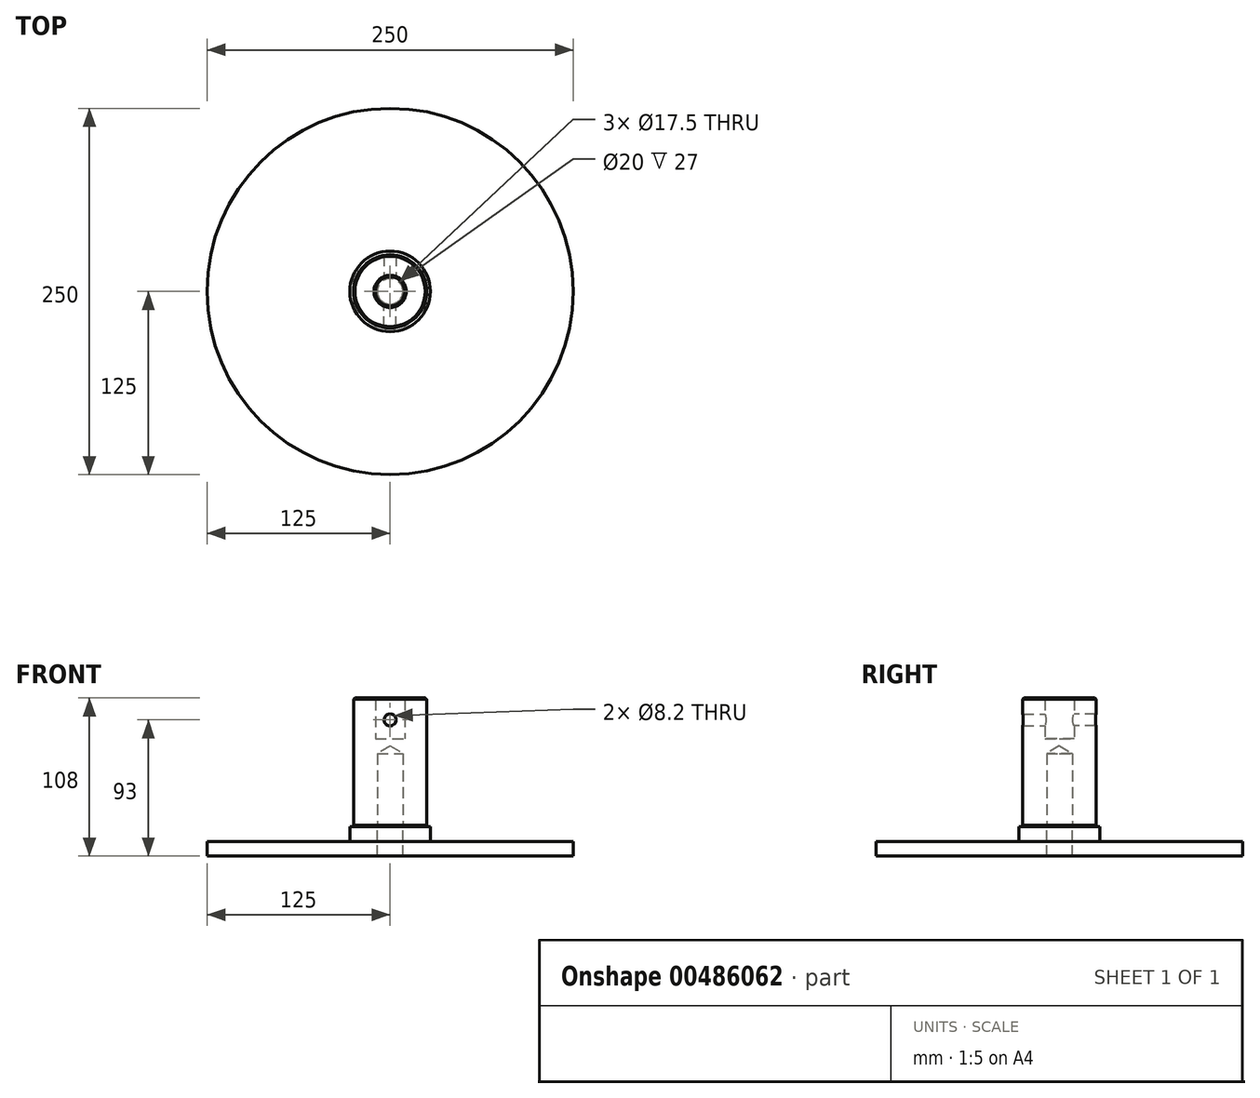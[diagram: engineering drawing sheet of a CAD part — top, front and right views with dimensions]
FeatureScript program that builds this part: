
annotation { "Feature Type Name" : "Feature", "Feature Type Description" : "" }
export const myFeature = defineFeature(function(context is Context, id is Id, definition is map)
    precondition{}
    {
        {
            var Q0;
            Q0=qCreatedBy(makeId("Front.planeOp"),FACE);
            var sketch = newSketch(context, id + "F0", { "sketchPlane" : qUnion([Q0])});
            skLineSegment(sketch, "E0.bottom", {"start": v(25, 0) * mm, "end": v(10, 0) * mm});
            skLineSegment(sketch, "E0.top", {"start": v(25, -48) * mm, "end": v(-25, -48) * mm});
            skLineSegment(sketch, "E0.left", {"start": v(25, 0) * mm, "end": v(25, -48) * mm});
            skLineSegment(sketch, "E0.right", {"start": v(-25, 0) * mm, "end": v(-25, -48) * mm});
            skLineSegment(sketch, "E1.top", {"start": v(10, -28) * mm, "end": v(-10, -28) * mm});
            skLineSegment(sketch, "E1.left", {"start": v(10, 0) * mm, "end": v(10, -28) * mm});
            skLineSegment(sketch, "E1.right", {"start": v(-10, 0) * mm, "end": v(-10, -28) * mm});
            skLineSegment(sketch, "E2", {"start": v(0, -137.33) * mm, "end": v(0, 23.92) * mm});
            skPoint(sketch, "E2.startSnap0", {"position": v(0, 0) * mm});
            skLineSegment(sketch, "E3.trimOffspring", {"start": v(-10, 0) * mm, "end": v(-25, 0) * mm});
            skPoint(sketch, "E4", {"position": v(0, -15) * mm});
            skLineSegment(sketch, "E5.bottom", {"start": v(-9.1, -48) * mm, "end": v(25, -48) * mm});
            skLineSegment(sketch, "E6.top", {"start": v(25, -88) * mm, "end": v(-25, -88) * mm});
            skLineSegment(sketch, "E6.left", {"start": v(25, -48) * mm, "end": v(25, -88) * mm});
            skLineSegment(sketch, "E6.right", {"start": v(-25, -48) * mm, "end": v(-25, -88) * mm});
            skSolve(sketch);
        }
        {
            var Q0;
            Q0=makeQuery(id+"F0.imprint","IMPRINT",FACE,{"disambiguationData":[TD([[makeQuery(id+"F0.imprint","IMPRINT",EDGE,{"derivedFrom":sQuery(id+"F0.wireOp",EDGE,"E0.bottom")}),1.0]])]});
            var Q1;
            Q1=sQuery(id+"F0.wireOp",EDGE,"E2");
            revolve(context, id + "F1", {"entities" : qUnion([Q0]), "axis" : qUnion([Q1]), "revolveType" : RevolveType.FULL});
        }
        {
            var Q0;
            Q0=makeQuery(id+"F1.opRevolve","SWEPT_EDGE",EDGE,{"disambiguationData":[OSD([sQuery(id+"F0.wireOp",EDGE,"E0.bottom"),sQuery(id+"F0.wireOp",EDGE,"E1.left")])]});
            var Q1;
            Q1=makeQuery(id+"F1.opRevolve","SWEPT_EDGE",EDGE,{"disambiguationData":[OSD([sQuery(id+"F0.wireOp",EDGE,"E0.bottom"),sQuery(id+"F0.wireOp",EDGE,"E0.left")])]});
            chamfer(context, id + "F2", {"entities" : qUnion([Q0, Q1]), "width" : 1 * mm, "tangentPropagation" : true});
        }
        {
            var Q0;
            Q0=sQuery(id+"F0.wireOp",VERTEX,"E4");
            var Q1;
            Q1=makeQuery(id+"F1.opRevolve","SWEPT_BODY",BODY,{"disambiguationData":[OSD([sQuery(id+"F0.wireOp",EDGE,"E0.bottom"),sQuery(id+"F0.wireOp",EDGE,"E0.top"),sQuery(id+"F0.wireOp",EDGE,"E0.left"),sQuery(id+"F0.wireOp",EDGE,"E1.top"),sQuery(id+"F0.wireOp",EDGE,"E1.left"),sQuery(id+"F0.wireOp",EDGE,"E2")])]});
            hole(context, id + "F3", {"style" : HoleStyle.SIMPLE, "endStyle" : HoleEndStyle.THROUGH, "oppositeDirection" : true, "standardTappedOrClearance" : lookupTablePath({ "standard" : "ISO", "size" : "8.2", "type" : "Drilled" }), "standardBlindInLast" : lookupTablePath({ "standard" : "ISO", "size" : "8.2", "type" : "Drilled" }), "holeDiameter" : 8.2 * mm, "isTappedThrough" : true, "tappedDepth" : 12 * mm, "tapClearance" : 3, "startFromSketch" : true, "locations" : qUnion([Q0]), "scope" : qUnion([Q1])});
        }
        {
            var Q0;
            Q0=sQuery(id+"F0.wireOp",VERTEX,"E4");
            var Q1;
            Q1=makeQuery(id+"F1.opRevolve","SWEPT_BODY",BODY,{"disambiguationData":[OSD([sQuery(id+"F0.wireOp",EDGE,"E0.bottom"),sQuery(id+"F0.wireOp",EDGE,"E0.top"),sQuery(id+"F0.wireOp",EDGE,"E0.left"),sQuery(id+"F0.wireOp",EDGE,"E1.top"),sQuery(id+"F0.wireOp",EDGE,"E1.left"),sQuery(id+"F0.wireOp",EDGE,"E2")])]});
            hole(context, id + "F4", {"style" : HoleStyle.SIMPLE, "endStyle" : HoleEndStyle.THROUGH, "standardTappedOrClearance" : lookupTablePath({ "standard" : "ISO", "size" : "8.2", "type" : "Drilled" }), "standardBlindInLast" : lookupTablePath({ "standard" : "ISO", "size" : "8.2", "type" : "Drilled" }), "holeDiameter" : 8.2 * mm, "isTappedThrough" : true, "tappedDepth" : 12 * mm, "tapClearance" : 3, "startFromSketch" : true, "locations" : qUnion([Q0]), "scope" : qUnion([Q1])});
        }
        {
            var Q0;
            {var subQ0=sQuery(id+"F0.wireOp",EDGE,"E6.right");Q0=makeQuery(id+"F0.imprint","IMPRINT",FACE,{"disambiguationData":[TD([[makeQuery(id+"F0.imprint","IMPRINT",EDGE,{"derivedFrom":subQ0}),1.0]])]});}
            var Q1;
            Q1=sQuery(id+"F0.wireOp",EDGE,"E2");
            revolve(context, id + "F5", {"operationType" : NewBodyOperationType.ADD, "entities" : qUnion([Q0]), "axis" : qUnion([Q1]), "revolveType" : RevolveType.FULL});
        }
        {
            var Q0;
            Q0=makeQuery(id+"F5.opRevolve","SWEPT_EDGE",EDGE,{"disambiguationData":[OSD([sQuery(id+"F0.wireOp",EDGE,"E6.top"),sQuery(id+"F0.wireOp",EDGE,"E6.left")])]});
            chamfer(context, id + "F6", {"entities" : qUnion([Q0]), "width" : 1 * mm, "tangentPropagation" : true});
        }
        {
            var Q0;
            Q0=makeQuery(id+"F5.opRevolve","SWEPT_FACE",FACE,{"disambiguationData":[OSD([sQuery(id+"F0.wireOp",EDGE,"E6.top")])]});
            var sketch = newSketch(context, id + "F7", { "sketchPlane" : qUnion([Q0])});
            skPoint(sketch, "E7", {"position": v(0, 0) * mm});
            skCircle(sketch, "E8", {"center": v(0, 0) * mm, "radius": 27.5 * mm});
            skSolve(sketch);
        }
        {
            var Q0;
            Q0=sQuery(id+"F7.wireOp",VERTEX,"E7");
            var Q1;
            Q1=makeQuery(id+"F1.opRevolve","SWEPT_BODY",BODY,{"disambiguationData":[OSD([sQuery(id+"F0.wireOp",EDGE,"E0.bottom"),sQuery(id+"F0.wireOp",EDGE,"E0.left"),sQuery(id+"F0.wireOp",EDGE,"E1.top"),sQuery(id+"F0.wireOp",EDGE,"E1.left"),sQuery(id+"F0.wireOp",EDGE,"E2"),sQuery(id+"F0.wireOp",EDGE,"E0.top")])]});
            hole(context, id + "F8", {"style" : HoleStyle.SIMPLE, "endStyle" : HoleEndStyle.BLIND, "standardTappedOrClearance" : lookupTablePath({ "standard" : "ISO", "engagement" : "75%", "pitch" : "2.5 mm", "size" : "M20", "type" : "Tapped" }), "standardBlindInLast" : lookupTablePath({ "standard" : "ISO", "engagement" : "75%", "pitch" : "2.5 mm", "size" : "M20", "type" : "Tapped" }), "holeDiameter" : 17.5 * mm, "majorDiameter" : 20 * mm, "showTappedDepth" : true, "holeDepth" : 50 * mm, "isTappedThrough" : true, "tappedDepth" : 42.5 * mm, "tapClearance" : 3, "startFromSketch" : true, "locations" : qUnion([Q0]), "scope" : qUnion([Q1])});
        }
        {
            var Q0;
            Q0 = qSketchRegion(id + "F7", true);
            extrude(context, id + "F9", {"entities" : qUnion([Q0]), "depth" : 10 * mm, "offsetDistance" : 25 * mm});
        }
        {
            var Q0;
            Q0=sQuery(id+"F7.wireOp",VERTEX,"E7");
            var Q1;
            Q1=makeQuery(id+"F9.opExtrude","SWEPT_BODY",BODY,{"disambiguationData":[OSD([sQuery(id+"F7.wireOp",EDGE,"E8")])]});
            hole(context, id + "F10", {"style" : HoleStyle.SIMPLE, "endStyle" : HoleEndStyle.BLIND, "oppositeDirection" : true, "standardTappedOrClearance" : lookupTablePath({ "standard" : "ISO", "engagement" : "75%", "pitch" : "2.5 mm", "size" : "M20", "type" : "Tapped" }), "standardBlindInLast" : lookupTablePath({ "standard" : "ISO", "engagement" : "75%", "pitch" : "2.5 mm", "size" : "M20", "type" : "Tapped" }), "holeDiameter" : 17.5 * mm, "majorDiameter" : 20 * mm, "showTappedDepth" : true, "holeDepth" : 50 * mm, "isTappedThrough" : true, "tappedDepth" : 42.5 * mm, "tapClearance" : 3, "startFromSketch" : true, "locations" : qUnion([Q0]), "scope" : qUnion([Q1])});
        }
        {
            var Q0;
            Q0=makeQuery(id+"F9.opExtrude","CAP_FACE",FACE,{"disambiguationData":[OSD([sQuery(id+"F7.wireOp",EDGE,"E8")])],"isStart":false});
            var sketch = newSketch(context, id + "F11", { "sketchPlane" : qUnion([Q0])});
            skCircle(sketch, "E9", {"center": v(0, 0) * mm, "radius": 125 * mm});
            skSolve(sketch);
        }
        {
            var Q0;
            Q0=makeQuery(id+"F11.imprint","IMPRINT",FACE,{"disambiguationData":[TD([[makeQuery(id+"F11.imprint","IMPRINT",EDGE,{"derivedFrom":sQuery(id+"F11.wireOp",EDGE,"E9")}),1.0]])]});
            var Q1;
            {var subQ0=sQuery(id+"F7.wireOp",EDGE,"E8");Q1=makeQuery(id+"F11.imprint","IMPRINT",FACE,{"disambiguationData":[TD([[makeQuery(id+"F11.imprint","IMPRINT",EDGE,{"derivedFrom":makeQuery(id+"F9.opExtrude","CAP_EDGE",EDGE,{"disambiguationData":[OSD([subQ0])],"isStart":false})}),1.0]])]});}
            var Q2;
            Q2=makeQuery(id+"F11.imprint","IMPRINT",FACE,{"disambiguationData":[TD([[makeQuery(id+"F11.imprint","IMPRINT",EDGE,{"derivedFrom":makeQuery(id+"F10.hole-0.boolean.opBoolean","INTERSECT",EDGE,{"derivedFrom":[makeQuery(id+"F9.opExtrude","CAP_FACE",FACE,{"disambiguationData":[OSD([sQuery(id+"F7.wireOp",EDGE,"E8")])],"isStart":false}),makeQuery(id+"F10.hole-0.opRevolve","SWEPT_FACE",FACE,{"disambiguationData":[OSD([sQuery(id+"F10.hole-0.sketch.wireOp",EDGE,"core_line_2")])]})]})}),-1.0]])]});
            extrude(context, id + "F12", {"entities" : qUnion([Q0, Q1, Q2]), "depth" : 10 * mm, "offsetDistance" : 25 * mm});
        }
    });
